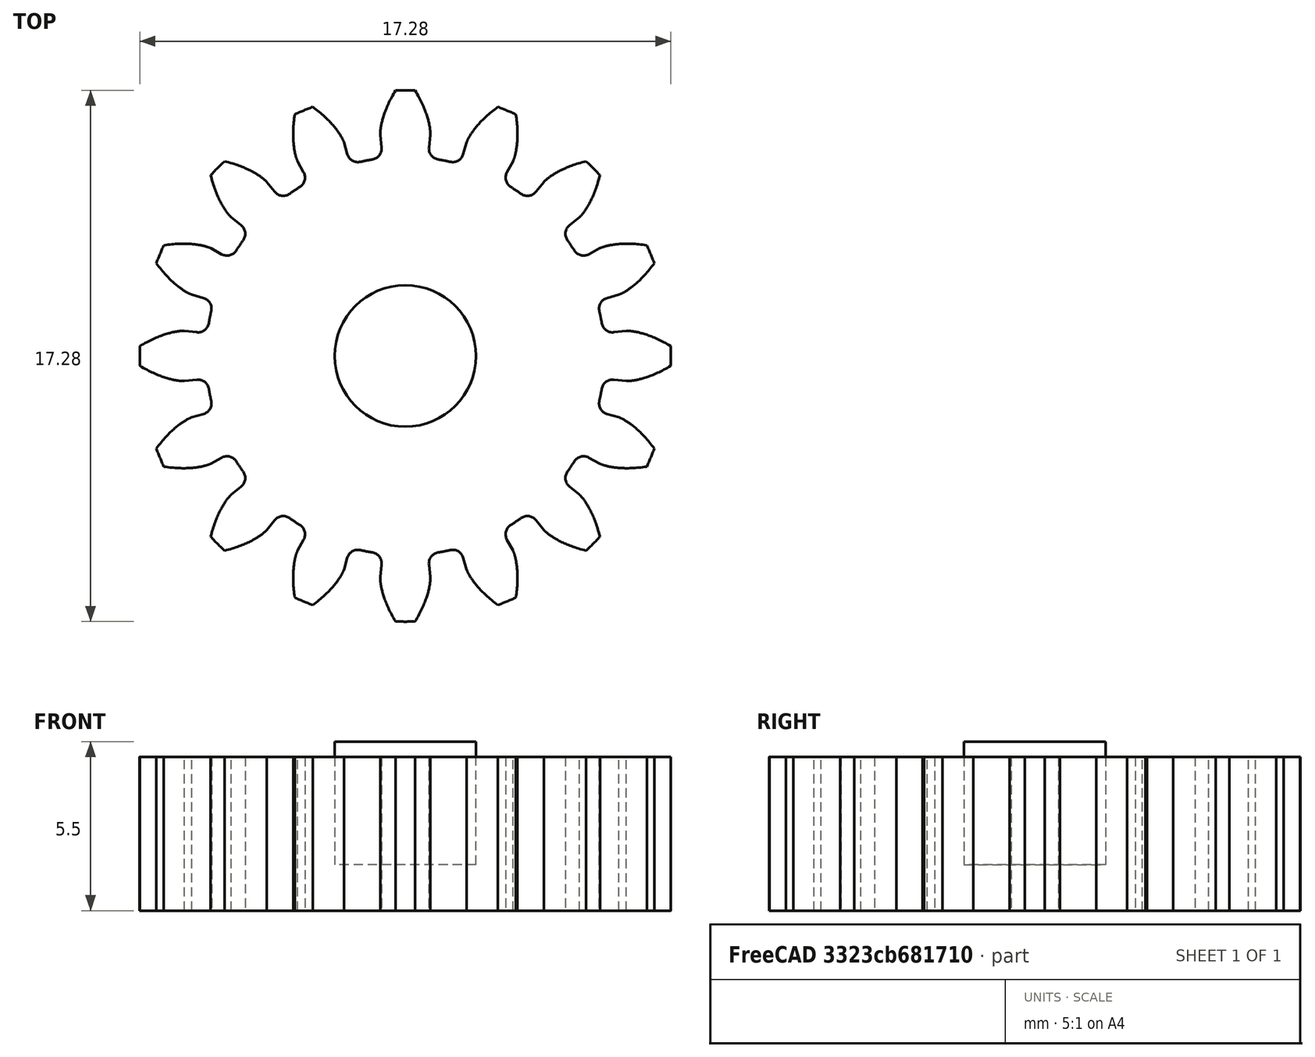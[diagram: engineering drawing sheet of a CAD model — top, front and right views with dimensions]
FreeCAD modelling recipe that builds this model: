
FCSTD DOCUMENT  (FreeCAD 0.20R29177 +426 (Git))
Label: servoGear
License: All rights reserved
LicenseURL: http://en.wikipedia.org/wiki/All_rights_reserved
objects: Mesh::Feature×1, Part::Part2DObjectPython×1, Part::Extrusion×1, Part::Cylinder×1
note: 3 computed .brp shape members not serialized (recipe doc carries the construction recipe); baked Part::Feature solids carry a one-line shape summary decoded from their .brp

FEATURE [Mesh::Feature] ServoGear
FEATURE [Part::Part2DObjectPython] InvoluteGear  # Draft 2D object (typed FeaturePython)
  ExternalGear = true
  HighPrecision = true
  Modules = 0.96
  NumberOfTeeth = 16
  PressureAngle = 20
FEATURE [Part::Extrusion] Extrude
  Base = -> InvoluteGear
  Dir = (0,0,1)
  DirMode = 2
  FaceMakerClass = Part::FaceMakerBullseye
  LengthFwd = 5
  LengthRev = 0
  Solid = true
  Symmetric = false
FEATURE [Part::Cylinder] Cylinder
  Angle = 360
  AttacherType = Attacher::AttachEngine3D
  FirstAngle = 0
  Height = 4
  Placement = pos=(0,0,1.5) rot=(0,0,1;0rad)
  Radius = 2.3
  SecondAngle = 0
